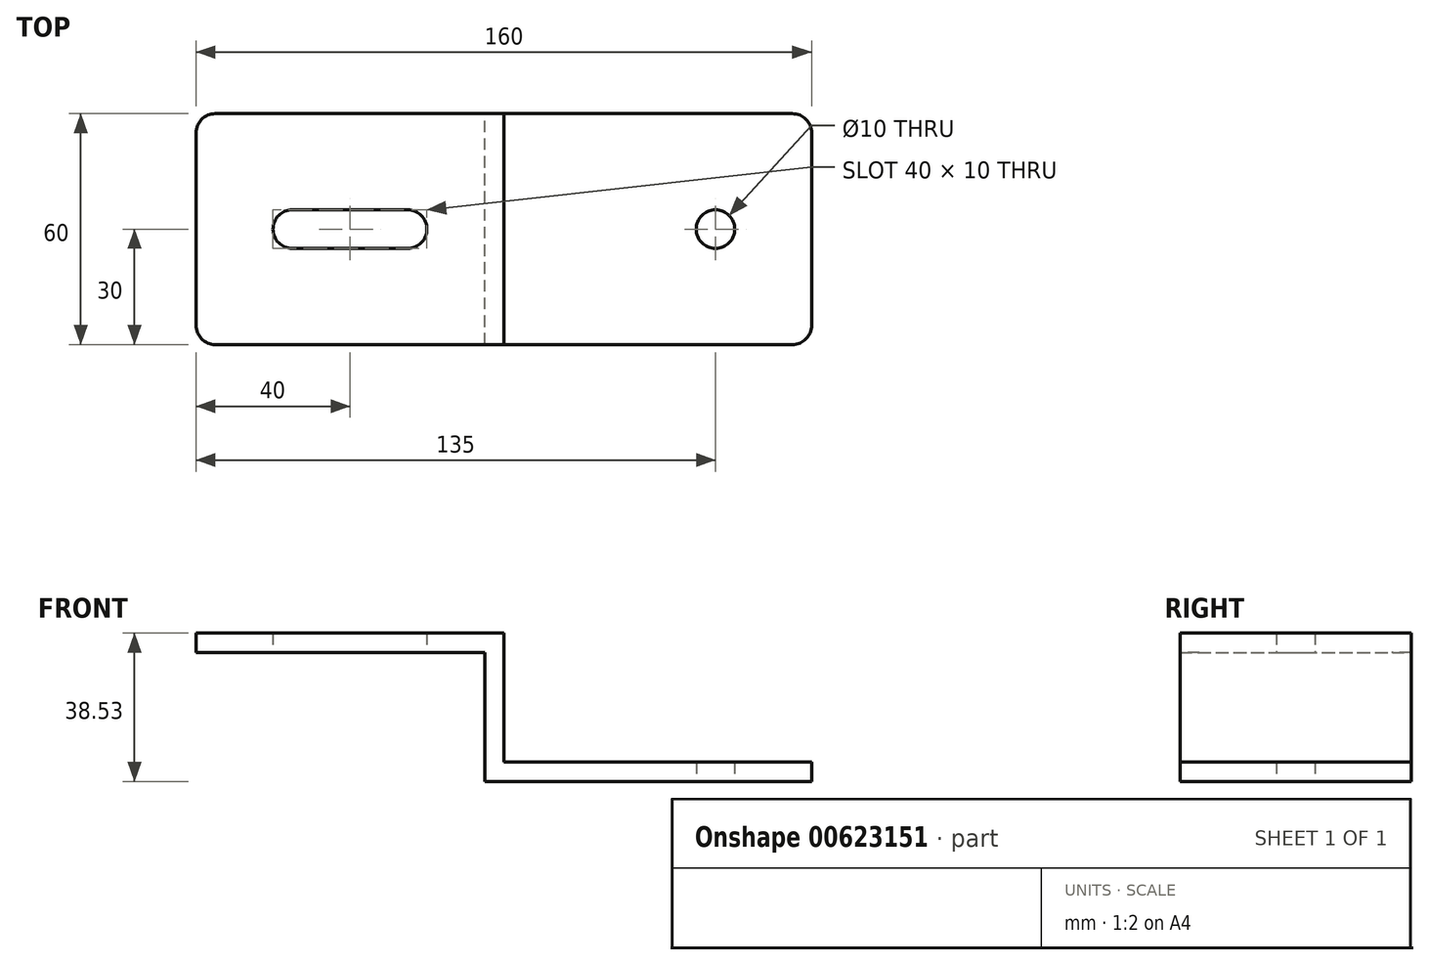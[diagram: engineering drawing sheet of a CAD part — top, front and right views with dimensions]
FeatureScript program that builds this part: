
annotation { "Feature Type Name" : "Feature", "Feature Type Description" : "" }
export const myFeature = defineFeature(function(context is Context, id is Id, definition is map)
    precondition{}
    {
        {
            var Q0;
            Q0=qCreatedBy(makeId("Front.planeOp"),FACE);
            var sketch = newSketch(context, id + "F0", { "sketchPlane" : qUnion([Q0])});
            skLineSegment(sketch, "E0", {"start": v(0, 0) * mm, "end": v(-80, 0) * mm});
            skLineSegment(sketch, "E1", {"start": v(-80, 0) * mm, "end": v(-80, 33.53) * mm});
            skLineSegment(sketch, "E2", {"start": v(-80, 33.53) * mm, "end": v(-160, 33.53) * mm});
            skLineSegment(sketch, "E3", {"start": v(-160, 33.53) * mm, "end": v(-160, 28.53) * mm});
            skLineSegment(sketch, "E4", {"start": v(-160, 28.53) * mm, "end": v(-85, 28.53) * mm});
            skLineSegment(sketch, "E5", {"start": v(-85, 28.53) * mm, "end": v(-85, -5) * mm});
            skLineSegment(sketch, "E6", {"start": v(-85, -5) * mm, "end": v(0, -5) * mm});
            skLineSegment(sketch, "E7", {"start": v(0, -5) * mm, "end": v(0, 0) * mm});
            skSolve(sketch);
        }
        {
            var Q0;
            Q0 = qSketchRegion(id + "F0", true);
            extrude(context, id + "F1", {"entities" : qUnion([Q0]), "depth" : 60 * mm, "offsetDistance" : 25 * mm});
        }
        {
            var Q0;
            Q0=makeQuery(id+"F1.opExtrude","SWEPT_FACE",FACE,{"disambiguationData":[OSD([sQuery(id+"F0.wireOp",EDGE,"E0")])]});
            var sketch = newSketch(context, id + "F2", { "sketchPlane" : qUnion([Q0])});
            skPoint(sketch, "E8", {"position": v(-25, -30) * mm});
            skPoint(sketch, "E8.positionSnap0", {"position": v(0, -30) * mm});
            skCircle(sketch, "E9", {"center": v(-25, -30) * mm, "radius": 5 * mm});
            skPoint(sketch, "E10", {"position": v(-120, -30) * mm});
            skPoint(sketch, "E11", {"position": v(-135, -30) * mm});
            skPoint(sketch, "E12", {"position": v(-105, -30) * mm});
            skArc(sketch, "E13", {"start": v(-135, -25) * mm, "mid": v(-140, -30) * mm, "end": v(-135, -35) * mm});
            skArc(sketch, "E14", {"start": v(-105, -35) * mm, "mid": v(-100, -30) * mm, "end": v(-105, -25) * mm});
            skPoint(sketch, "E15", {"position": v(-135, -25) * mm});
            skPoint(sketch, "E16", {"position": v(-135, -35) * mm});
            skPoint(sketch, "E17", {"position": v(-105, -25) * mm});
            skPoint(sketch, "E18", {"position": v(-105, -35) * mm});
            skLineSegment(sketch, "E19", {"start": v(-135, -25) * mm, "end": v(-105, -25) * mm});
            skLineSegment(sketch, "E20", {"start": v(-135, -35) * mm, "end": v(-105, -35) * mm});
            skSolve(sketch);
        }
        {
            var Q0;
            Q0 = qSketchRegion(id + "F2", true);
            extrude(context, id + "F3", {"entities" : qUnion([Q0]), "operationType" : NewBodyOperationType.REMOVE, "depth" : 100 * mm, "offsetDistance" : 25 * mm, "symmetric" : true});
        }
        {
            var Q0;
            Q0=makeQuery(id+"F1.opExtrude","CAP_EDGE",EDGE,{"disambiguationData":[OSD([sQuery(id+"F0.wireOp",EDGE,"E3")])],"isStart":false});
            var Q1;
            Q1=makeQuery(id+"F1.opExtrude","CAP_EDGE",EDGE,{"disambiguationData":[OSD([sQuery(id+"F0.wireOp",EDGE,"E3")])],"isStart":true});
            var Q2;
            Q2=makeQuery(id+"F1.opExtrude","CAP_EDGE",EDGE,{"disambiguationData":[OSD([sQuery(id+"F0.wireOp",EDGE,"E7")])],"isStart":false});
            var Q3;
            Q3=makeQuery(id+"F1.opExtrude","CAP_EDGE",EDGE,{"disambiguationData":[OSD([sQuery(id+"F0.wireOp",EDGE,"E7")])],"isStart":true});
            fillet(context, id + "F4", {"entities" : qUnion([Q0, Q1, Q2, Q3]), "radius" : 5 * mm, "tangentPropagation" : true, "allowEdgeOverflow" : false});
        }
    });
